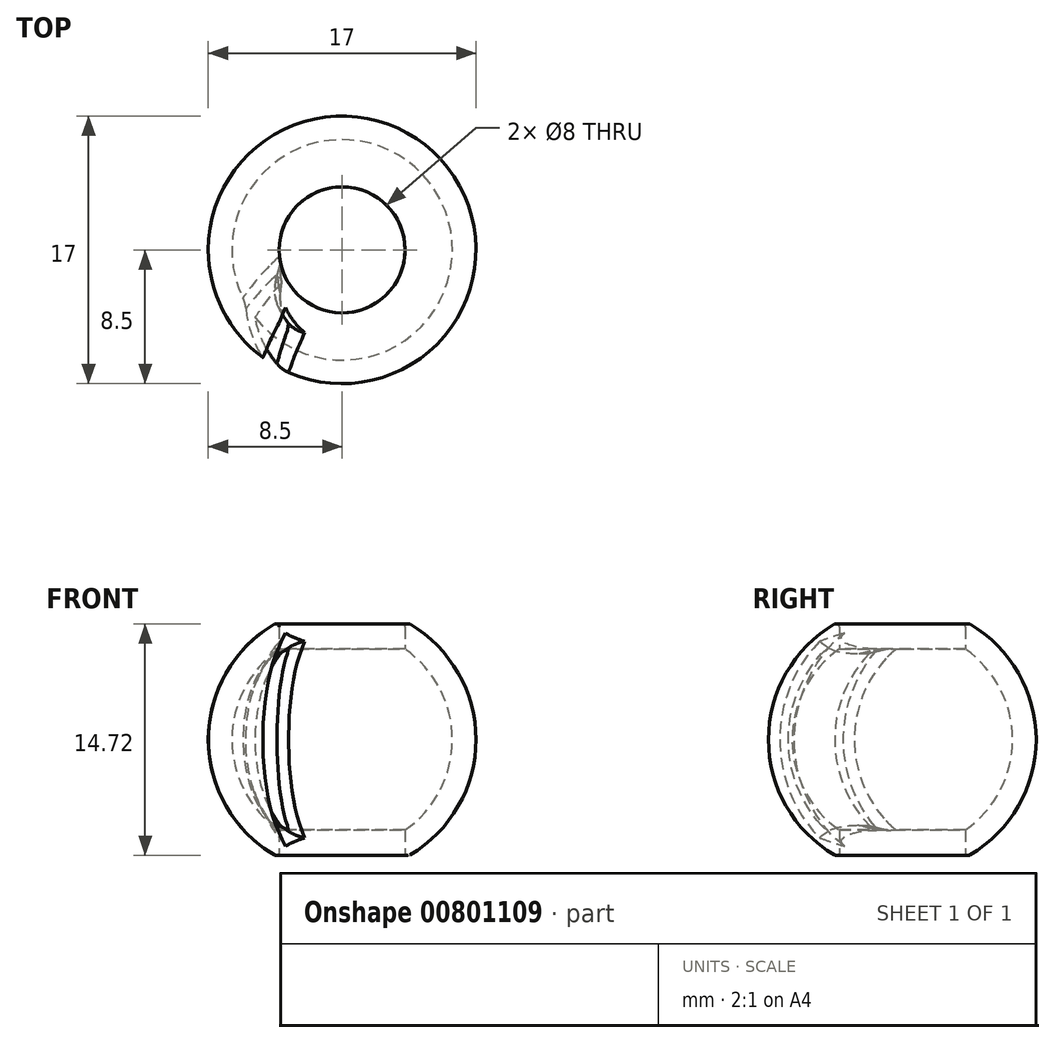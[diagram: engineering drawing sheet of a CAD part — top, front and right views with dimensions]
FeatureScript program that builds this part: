
annotation { "Feature Type Name" : "Feature", "Feature Type Description" : "" }
export const myFeature = defineFeature(function(context is Context, id is Id, definition is map)
    precondition{}
    {
        {
            var Q0;
            Q0=qCreatedBy(makeId("Front.planeOp"),FACE);
            var sketch = newSketch(context, id + "F0", { "sketchPlane" : qUnion([Q0])});
            skLineSegment(sketch, "E0", {"start": v(-8.75, 17.5) * mm, "end": v(-8.75, -5.75) * mm});
            skLineSegment(sketch, "E1", {"start": v(0, -11.86) * mm, "end": v(0, 26.29) * mm, "construction": true});
            skSolve(sketch);
        }
        {
            var Q0;
            Q0=qCreatedBy(makeId("Front.planeOp"),FACE);
            var sketch = newSketch(context, id + "F1", { "sketchPlane" : qUnion([Q0])});
            skArc(sketch, "E2", {"start": v(-4, 7.5) * mm, "mid": v(-8.5, 0) * mm, "end": v(-4, -7.5) * mm});
            skLineSegment(sketch, "E3", {"start": v(0, 7.5) * mm, "end": v(0, -7.5) * mm});
            skLineSegment(sketch, "E4", {"start": v(0, 14.75) * mm, "end": v(0, 8.5) * mm, "construction": true});
            skLineSegment(sketch, "E5", {"start": v(0, 7.5) * mm, "end": v(-4, 7.5) * mm});
            skLineSegment(sketch, "E6", {"start": v(-4, -7.5) * mm, "end": v(0, -7.5) * mm});
            skLineSegment(sketch, "E7.trimOffspring", {"start": v(0, 7.5) * mm, "end": v(0, -7.5) * mm, "construction": true});
            skLineSegment(sketch, "E8.trimOffspring", {"start": v(0, -8.5) * mm, "end": v(0, -15.94) * mm, "construction": true});
            skSolve(sketch);
        }
        {
            var Q0;
            Q0=qSketchRegion(id+"F1",true);
            var Q1;
            Q1=sQuery(id+"F0.wireOp",EDGE,"E1");
            revolve(context, id + "F2", {"surfaceOperationType" : NewSurfaceOperationType.NEW, "entities" : qUnion([Q0]), "axis" : qUnion([Q1]), "revolveType" : RevolveType.FULL});
        }
        {
            var Q0;
            Q0=makeQuery(id+"F2.opRevolve","SWEPT_FACE",FACE,{"disambiguationData":[OSD([sQuery(id+"F1.wireOp",EDGE,"4db80379-cc64-4494-b897-e08872da2e8e0.MirrorCS")])]});
            var Q1;
            Q1=makeQuery(id+"F2.opRevolve","SWEPT_FACE",FACE,{"disambiguationData":[OSD([sQuery(id+"F1.wireOp",EDGE,"AEIb5Jnk-OBmj-mYYU-YIDr-AcmcBF9XRxGy")])]});
            var Q2;
            Q2=makeQuery(id+"F2.opRevolve","SWEPT_BODY",BODY,{"disambiguationData":[OSD([sQuery(id+"F1.wireOp",EDGE,"E2"),sQuery(id+"F1.wireOp",EDGE,"E3"),sQuery(id+"F1.wireOp",EDGE,"E5"),sQuery(id+"F1.wireOp",EDGE,"E6")])]});
            shell(context, id + "F3", {"isHollow" : true, "entities" : qUnion([Q0, Q1]), "parts" : qUnion([Q2]), "thickness" : 1.5 * mm});
        }
        {
            var Q0;
            Q0=makeQuery(id+"F2.opRevolve","SWEPT_FACE",FACE,{"disambiguationData":[OSD([sQuery(id+"F1.wireOp",EDGE,"E6")])]});
            var sketch = newSketch(context, id + "F4", { "sketchPlane" : qUnion([Q0])});
            skCircle(sketch, "E9.0", {"center": v(0, 0) * mm, "radius": 4 * mm});
            skSolve(sketch);
        }
        {
            var Q0;
            Q0=qSketchRegion(id+"F4",true);
            extrude(context, id + "F5", {"entities" : qUnion([Q0]), "operationType" : NewBodyOperationType.REMOVE, "endBound" : BoundingType.THROUGH_ALL, "oppositeDirection" : true, "depth" : 25 * mm, "offsetDistance" : 25 * mm});
        }
        {
            var Q0;
            Q0=qCreatedBy(makeId("Top.planeOp"),FACE);
            var sketch = newSketch(context, id + "F6", { "sketchPlane" : qUnion([Q0])});
            skArc(sketch, "E10", {"start": v(0, 3.88) * mm, "mid": v(-3.87, 2.1) * mm, "end": v(-5.98, -1.6) * mm});
            skArc(sketch, "E11", {"start": v(-5.98, -1.6) * mm, "mid": v(-5.47, -6.06) * mm, "end": v(-2.35, -9.3) * mm});
            skArc(sketch, "E12", {"start": v(-2.35, -9.3) * mm, "mid": v(-1.2, -9.76) * mm, "end": v(0, -10.02) * mm});
            skSolve(sketch);
        }
        {
            var Q0;
            Q0=qCreatedBy(makeId("Right.planeOp"),FACE);
            var sketch = newSketch(context, id + "F7", { "sketchPlane" : qUnion([Q0])});
            skArc(sketch, "E13", {"start": v(-9.52, 0) * mm, "mid": v(-9.08, -2.86) * mm, "end": v(-7.8, -5.46) * mm});
            skArc(sketch, "E14.0", {"start": v(-10.02, 0) * mm, "mid": v(-9.56, -3.01) * mm, "end": v(-8.21, -5.75) * mm});
            skLineSegment(sketch, "E15", {"start": v(-12.89, 0) * mm, "end": v(-5.13, 0) * mm, "construction": true});
            skArc(sketch, "E16.MirrorCS", {"start": v(-9.52, 0) * mm, "mid": v(-9.08, 2.86) * mm, "end": v(-7.8, 5.46) * mm});
            skArc(sketch, "E17.MirrorCS", {"start": v(-10.02, 0) * mm, "mid": v(-9.56, 3.01) * mm, "end": v(-8.21, 5.75) * mm});
            skPoint(sketch, "E18", {"position": v(-11.2, 0) * mm});
            skLineSegment(sketch, "E19", {"start": v(-8.21, -5.75) * mm, "end": v(-7.8, -5.46) * mm});
            skLineSegment(sketch, "E20", {"start": v(-8.21, 5.75) * mm, "end": v(-7.8, 5.46) * mm});
            skSolve(sketch);
        }
        {
            var Q0;
            Q0=makeQuery(id+"F7.imprint","IMPRINT",FACE,{"disambiguationData":[TD([[makeQuery(id+"F7.imprint","IMPRINT",EDGE,{"derivedFrom":sQuery(id+"F7.wireOp",EDGE,"E13")}),-1.0]])]});
            var Q1;
            Q1=sQuery(id+"F6.wireOp",EDGE,"E12");
            var Q2;
            Q2=sQuery(id+"F6.wireOp",EDGE,"E11");
            var Q3;
            Q3=sQuery(id+"F6.wireOp",EDGE,"E10");
            sweep(context, id + "F8", {"operationType" : NewBodyOperationType.REMOVE, "profiles" : qUnion([Q0]), "path" : qUnion([Q1, Q2, Q3])});
        }
        {
            var Q0;
            Q0=makeQuery(id+"F8.boolean.opBoolean","INTERSECT",EDGE,{"derivedFrom":[makeQuery(id+"F2.opRevolve","SWEPT_FACE",FACE,{"disambiguationData":[OSD([sQuery(id+"F1.wireOp",EDGE,"E2")])]}),makeQuery(id+"F8.opSweep","SWEPT_FACE",FACE,{"disambiguationData":[OSD([sQuery(id+"F6.wireOp",EDGE,"E11"),sQuery(id+"F7.wireOp",EDGE,"E19")])]})]});
            var Q1;
            Q1=makeQuery(id+"F8.boolean.opBoolean","INTERSECT",EDGE,{"derivedFrom":[makeQuery(id+"F2.opRevolve","SWEPT_FACE",FACE,{"disambiguationData":[OSD([sQuery(id+"F1.wireOp",EDGE,"E2")])]}),makeQuery(id+"F8.opSweep","SWEPT_FACE",FACE,{"disambiguationData":[OSD([sQuery(id+"F6.wireOp",EDGE,"E11"),sQuery(id+"F7.wireOp",EDGE,"E20")])]})]});
            fillet(context, id + "F9", {"entities" : qUnion([Q0, Q1]), "radius" : 0.9 * mm, "tangentPropagation" : true, "allowEdgeOverflow" : false});
        }
        {
            var Q0;
            Q0=makeQuery(id+"F8.boolean.opBoolean","INTERSECT",EDGE,{"derivedFrom":[makeQuery(id+"F3.opShell","OFFSET_FACE",FACE,{"disambiguationData":[OSD([sQuery(id+"F1.wireOp",EDGE,"E2")])]}),makeQuery(id+"F8.opSweep","SWEPT_FACE",FACE,{"disambiguationData":[OSD([sQuery(id+"F6.wireOp",EDGE,"E11"),sQuery(id+"F7.wireOp",EDGE,"E14.0"),sQuery(id+"F7.wireOp",EDGE,"E17.MirrorCS")])]})]});
            var Q1;
            Q1=makeQuery(id+"F8.boolean.opBoolean","INTERSECT",EDGE,{"derivedFrom":[makeQuery(id+"F2.opRevolve","SWEPT_FACE",FACE,{"disambiguationData":[OSD([sQuery(id+"F1.wireOp",EDGE,"E2")])]}),makeQuery(id+"F8.opSweep","SWEPT_FACE",FACE,{"disambiguationData":[OSD([sQuery(id+"F6.wireOp",EDGE,"E11"),sQuery(id+"F7.wireOp",EDGE,"E13"),sQuery(id+"F7.wireOp",EDGE,"E16.MirrorCS")])]})]});
            fillet(context, id + "F10", {"entities" : qUnion([Q0, Q1]), "radius" : 2 * mm, "tangentPropagation" : true, "allowEdgeOverflow" : false});
        }
        {
            var Q0;
            Q0=makeQuery(id+"F2.opRevolve","SWEPT_EDGE",EDGE,{"disambiguationData":[OSD([sQuery(id+"F1.wireOp",EDGE,"E2"),sQuery(id+"F1.wireOp",EDGE,"E5")])]});
            fillet(context, id + "F11", {"entities" : qUnion([Q0]), "radius" : 0.2 * mm, "tangentPropagation" : true, "allowEdgeOverflow" : false});
        }
        {
            var Q0;
            Q0=makeQuery(id+"F5.boolean.opBoolean","MERGE",EDGE,{"derivedFrom":[makeQuery(id+"F2.opRevolve","SWEPT_EDGE",EDGE,{"disambiguationData":[OSD([sQuery(id+"F1.wireOp",EDGE,"E2"),sQuery(id+"F1.wireOp",EDGE,"E6")])]}),makeQuery(id+"F5.opExtrude","CAP_EDGE",EDGE,{"disambiguationData":[OSD([sQuery(id+"F4.wireOp",EDGE,"E9.0")])],"isStart":true})]});
            fillet(context, id + "F12", {"entities" : qUnion([Q0]), "radius" : 0.2 * mm, "tangentPropagation" : true, "allowEdgeOverflow" : false});
        }
    });
